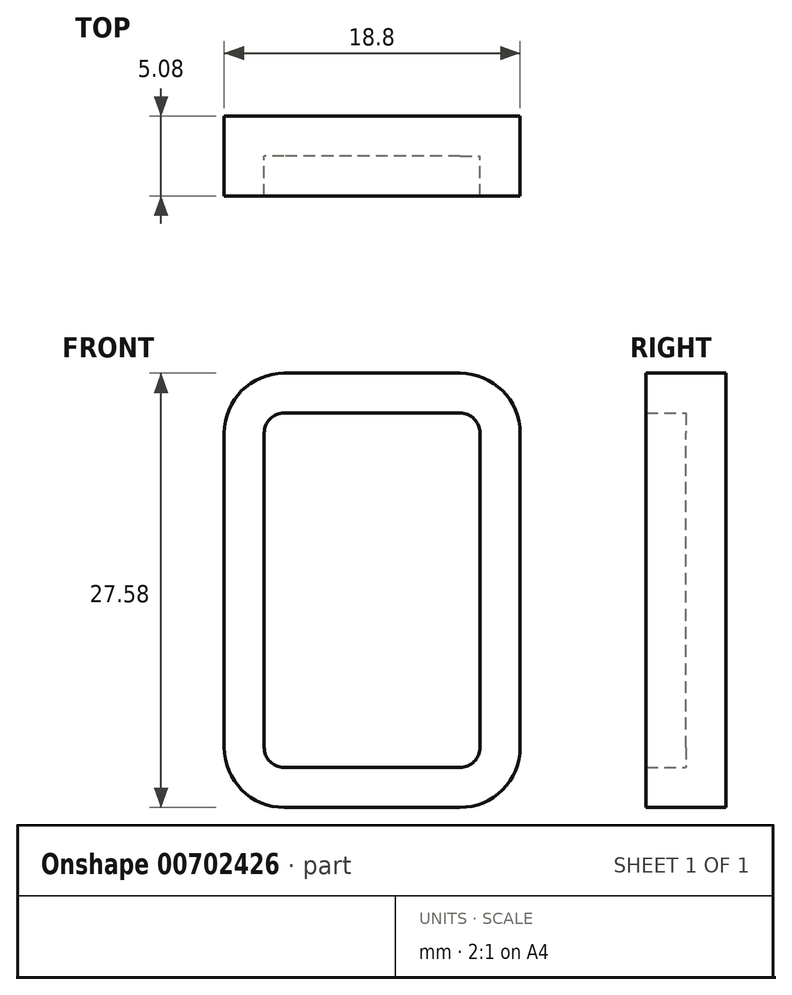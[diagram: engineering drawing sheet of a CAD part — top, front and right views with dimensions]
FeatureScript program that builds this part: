
annotation { "Feature Type Name" : "Feature", "Feature Type Description" : "" }
export const myFeature = defineFeature(function(context is Context, id is Id, definition is map)
    precondition{}
    {
        {
            var Q0;
            Q0=qCreatedBy(makeId("Front.planeOp"),FACE);
            var sketch = newSketch(context, id + "F0", { "sketchPlane" : qUnion([Q0])});
            skLineSegment(sketch, "E0.bottom", {"start": v(5.59, -13.8) * mm, "end": v(-5.59, -13.8) * mm});
            skLineSegment(sketch, "E0.top", {"start": v(5.59, 13.8) * mm, "end": v(-5.59, 13.8) * mm});
            skLineSegment(sketch, "E0.left", {"start": v(9.4, -9.98) * mm, "end": v(9.4, 9.98) * mm});
            skLineSegment(sketch, "E0.right", {"start": v(-9.4, -9.98) * mm, "end": v(-9.4, 9.98) * mm});
            skPoint(sketch, "E0.middle", {"position": v(0, 0) * mm});
            skPoint(sketch, "E1.visualSharp", {"position": v(-9.4, 13.8) * mm});
            skArc(sketch, "E1.filletArc", {"start": v(-5.59, 13.8) * mm, "mid": v(-8.28, 12.68) * mm, "end": v(-9.4, 9.98) * mm});
            skPoint(sketch, "E2.visualSharp", {"position": v(9.4, 13.8) * mm});
            skArc(sketch, "E2.filletArc", {"start": v(9.4, 9.98) * mm, "mid": v(8.28, 12.68) * mm, "end": v(5.59, 13.8) * mm});
            skPoint(sketch, "E3.visualSharp", {"position": v(-9.4, -13.8) * mm});
            skArc(sketch, "E3.filletArc", {"start": v(-9.4, -9.98) * mm, "mid": v(-8.28, -12.68) * mm, "end": v(-5.59, -13.8) * mm});
            skPoint(sketch, "E4.visualSharp", {"position": v(9.4, -13.8) * mm});
            skArc(sketch, "E4.filletArc", {"start": v(5.59, -13.8) * mm, "mid": v(8.28, -12.68) * mm, "end": v(9.4, -9.98) * mm});
            skSolve(sketch);
        }
        {
            var Q0;
            Q0 = qSketchRegion(id + "F0", true);
            extrude(context, id + "F1", {"entities" : qUnion([Q0]), "depth" : 5.08 * mm, "offsetDistance" : 25.4 * mm});
        }
        {
            var Q0;
            Q0=makeQuery(id+"F1.opExtrude","CAP_FACE",FACE,{"disambiguationData":[OSD([sQuery(id+"F0.wireOp",EDGE,"E0.bottom"),sQuery(id+"F0.wireOp",EDGE,"E0.top"),sQuery(id+"F0.wireOp",EDGE,"E0.left"),sQuery(id+"F0.wireOp",EDGE,"E0.right"),sQuery(id+"F0.wireOp",EDGE,"E1.filletArc"),sQuery(id+"F0.wireOp",EDGE,"E2.filletArc"),sQuery(id+"F0.wireOp",EDGE,"E3.filletArc"),sQuery(id+"F0.wireOp",EDGE,"E4.filletArc")])],"isStart":false});
            shell(context, id + "F2", {"entities" : qUnion([Q0]), "thickness" : 2.54 * mm});
        }
    });
